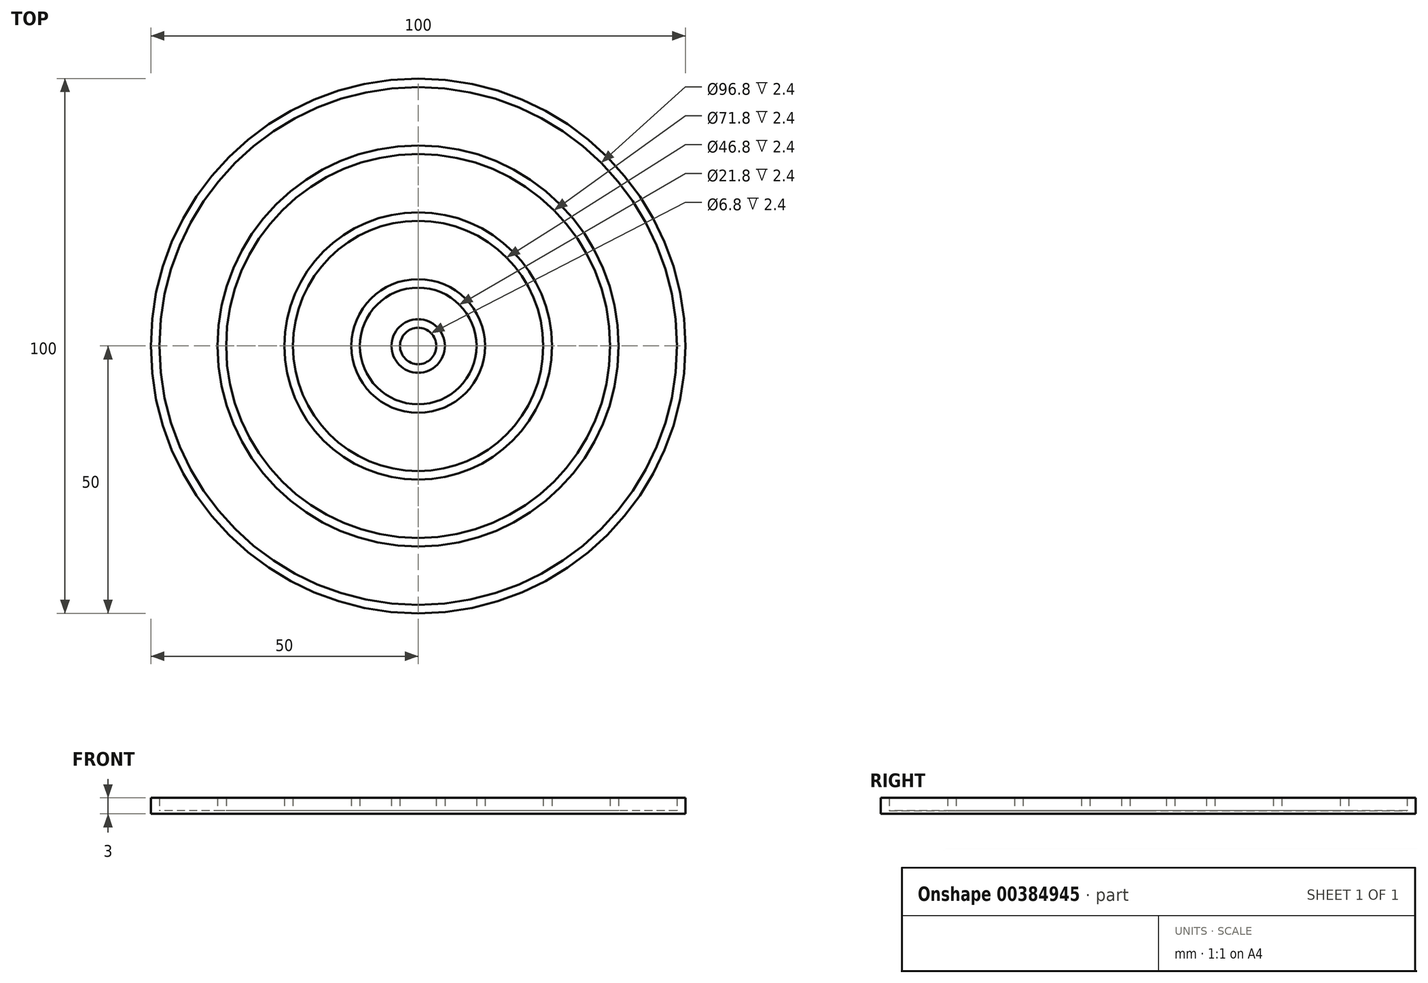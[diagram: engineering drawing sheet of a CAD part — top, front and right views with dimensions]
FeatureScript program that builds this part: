
annotation { "Feature Type Name" : "Feature", "Feature Type Description" : "" }
export const myFeature = defineFeature(function(context is Context, id is Id, definition is map)
    precondition{}
    {
        {
            var Q0;
            Q0=qCreatedBy(makeId("Top.planeOp"),FACE);
            var sketch = newSketch(context, id + "F0", { "sketchPlane" : qUnion([Q0])});
            skCircle(sketch, "E0", {"center": v(0, 0) * mm, "radius": 50 * mm});
            skCircle(sketch, "E1", {"center": v(0, 0) * mm, "radius": 37.5 * mm});
            skCircle(sketch, "E2", {"center": v(0, 0) * mm, "radius": 25 * mm});
            skCircle(sketch, "E3", {"center": v(0, 0) * mm, "radius": 12.5 * mm});
            skCircle(sketch, "E4", {"center": v(0, 0) * mm, "radius": 5 * mm});
            skCircle(sketch, "E5.0", {"center": v(0, 0) * mm, "radius": 48.4 * mm});
            skCircle(sketch, "E6.0", {"center": v(0, 0) * mm, "radius": 35.9 * mm});
            skCircle(sketch, "E7.0", {"center": v(0, 0) * mm, "radius": 23.4 * mm});
            skCircle(sketch, "E8.0", {"center": v(0, 0) * mm, "radius": 10.9 * mm});
            skCircle(sketch, "E9.0", {"center": v(0, 0) * mm, "radius": 3.4 * mm});
            skSolve(sketch);
        }
        {
            var Q0;
            Q0=makeQuery(id+"F0.imprint","IMPRINT",FACE,{"disambiguationData":[TD([[makeQuery(id+"F0.imprint","IMPRINT",EDGE,{"derivedFrom":sQuery(id+"F0.wireOp",EDGE,"E0")}),1.0]])]});
            var Q1;
            Q1=makeQuery(id+"F0.imprint","IMPRINT",FACE,{"disambiguationData":[TD([[makeQuery(id+"F0.imprint","IMPRINT",EDGE,{"derivedFrom":sQuery(id+"F0.wireOp",EDGE,"E1")}),1.0]])]});
            var Q2;
            Q2=makeQuery(id+"F0.imprint","IMPRINT",FACE,{"disambiguationData":[TD([[makeQuery(id+"F0.imprint","IMPRINT",EDGE,{"derivedFrom":sQuery(id+"F0.wireOp",EDGE,"E2")}),1.0]])]});
            var Q3;
            Q3=makeQuery(id+"F0.imprint","IMPRINT",FACE,{"disambiguationData":[TD([[makeQuery(id+"F0.imprint","IMPRINT",EDGE,{"derivedFrom":sQuery(id+"F0.wireOp",EDGE,"E3")}),1.0]])]});
            var Q4;
            Q4=makeQuery(id+"F0.imprint","IMPRINT",FACE,{"disambiguationData":[TD([[makeQuery(id+"F0.imprint","IMPRINT",EDGE,{"derivedFrom":sQuery(id+"F0.wireOp",EDGE,"E4")}),1.0]])]});
            extrude(context, id + "F1", {"entities" : qUnion([Q0, Q1, Q2, Q3, Q4]), "depth" : 3 * mm});
        }
        {
            var Q0;
            Q0=makeQuery(id+"F0.imprint","IMPRINT",FACE,{"disambiguationData":[TD([[makeQuery(id+"F0.imprint","IMPRINT",EDGE,{"derivedFrom":sQuery(id+"F0.wireOp",EDGE,"E1")}),-1.0]])]});
            var Q1;
            Q1=makeQuery(id+"F0.imprint","IMPRINT",FACE,{"disambiguationData":[TD([[makeQuery(id+"F0.imprint","IMPRINT",EDGE,{"derivedFrom":sQuery(id+"F0.wireOp",EDGE,"E2")}),-1.0]])]});
            var Q2;
            Q2=makeQuery(id+"F0.imprint","IMPRINT",FACE,{"disambiguationData":[TD([[makeQuery(id+"F0.imprint","IMPRINT",EDGE,{"derivedFrom":sQuery(id+"F0.wireOp",EDGE,"E3")}),-1.0]])]});
            var Q3;
            Q3=makeQuery(id+"F0.imprint","IMPRINT",FACE,{"disambiguationData":[TD([[makeQuery(id+"F0.imprint","IMPRINT",EDGE,{"derivedFrom":sQuery(id+"F0.wireOp",EDGE,"E4")}),-1.0]])]});
            var Q4;
            Q4=makeQuery(id+"F0.imprint","IMPRINT",FACE,{"disambiguationData":[TD([[makeQuery(id+"F0.imprint","IMPRINT",EDGE,{"derivedFrom":sQuery(id+"F0.wireOp",EDGE,"E9.0")}),1.0]])]});
            extrude(context, id + "F2", {"entities" : qUnion([Q0, Q1, Q2, Q3, Q4]), "operationType" : NewBodyOperationType.ADD, "depth" : .6 * mm});
        }
    });
